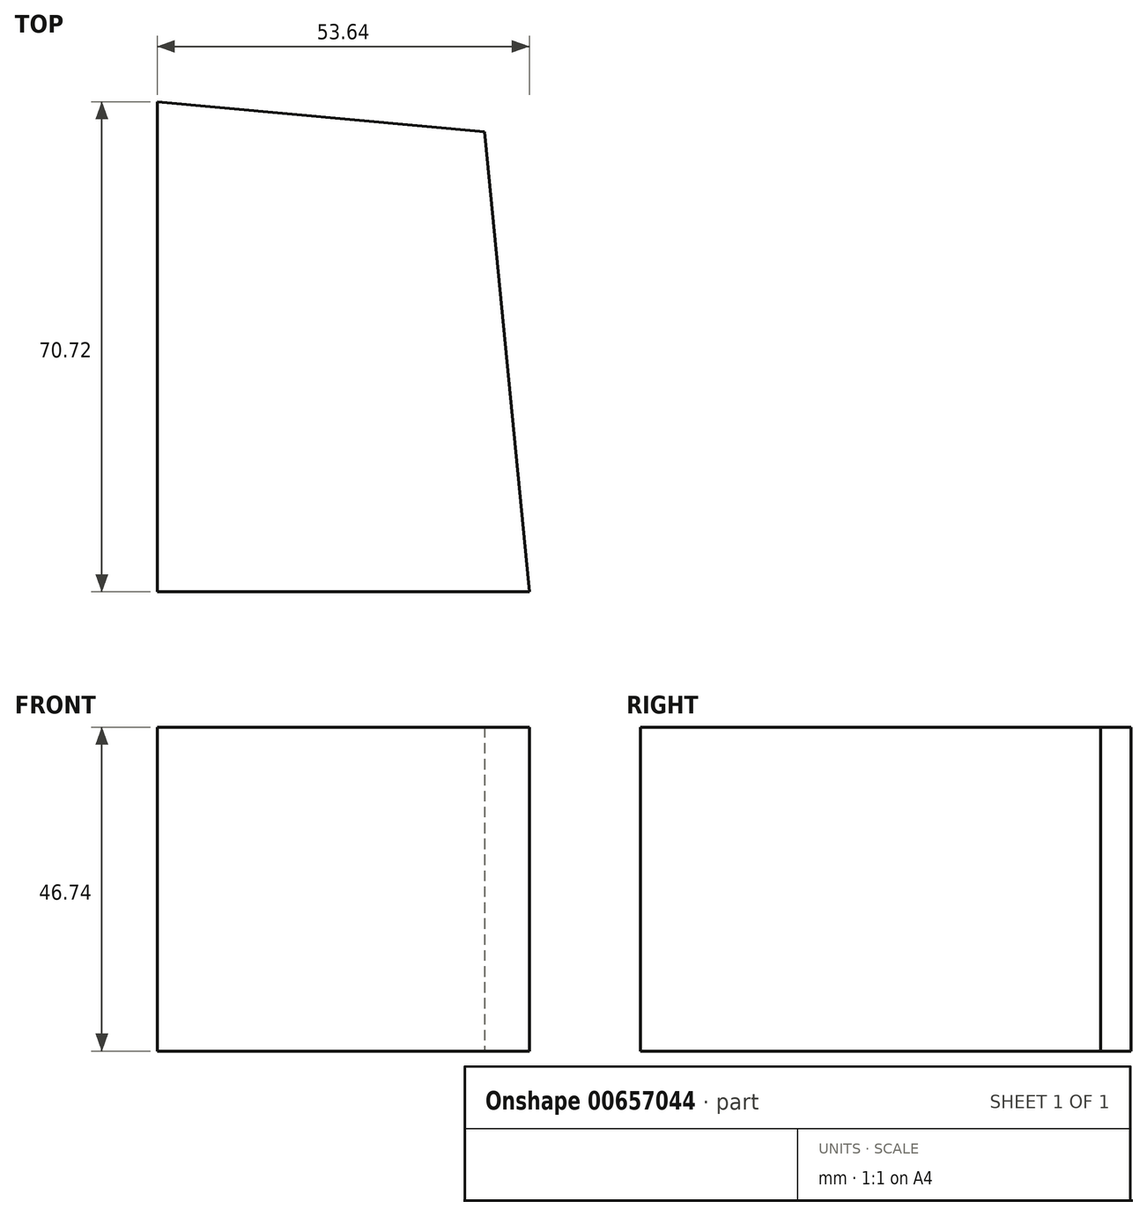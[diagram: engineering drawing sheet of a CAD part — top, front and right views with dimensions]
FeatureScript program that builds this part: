
annotation { "Feature Type Name" : "Feature", "Feature Type Description" : "" }
export const myFeature = defineFeature(function(context is Context, id is Id, definition is map)
    precondition{}
    {
        {
            var Q0;
            Q0=qCreatedBy(makeId("Top.planeOp"),FACE);
            var sketch = newSketch(context, id + "F0", { "sketchPlane" : qUnion([Q0])});
            skLineSegment(sketch, "E0", {"start": v(90.32, 70.72) * mm, "end": v(90.32, 0) * mm});
            skLineSegment(sketch, "E1", {"start": v(90.32, 0) * mm, "end": v(143.96, 0) * mm});
            skLineSegment(sketch, "E2", {"start": v(143.96, 0) * mm, "end": v(137.51, 66.36) * mm});
            skLineSegment(sketch, "E3", {"start": v(137.51, 66.36) * mm, "end": v(90.32, 70.72) * mm});
            skSolve(sketch);
        }
        {
            var Q0;
            Q0 = qSketchRegion(id + "F0", true);
            extrude(context, id + "F1", {"entities" : qUnion([Q0]), "depth" : 46.74 * mm, "offsetDistance" : 25.4 * mm});
        }
    });
